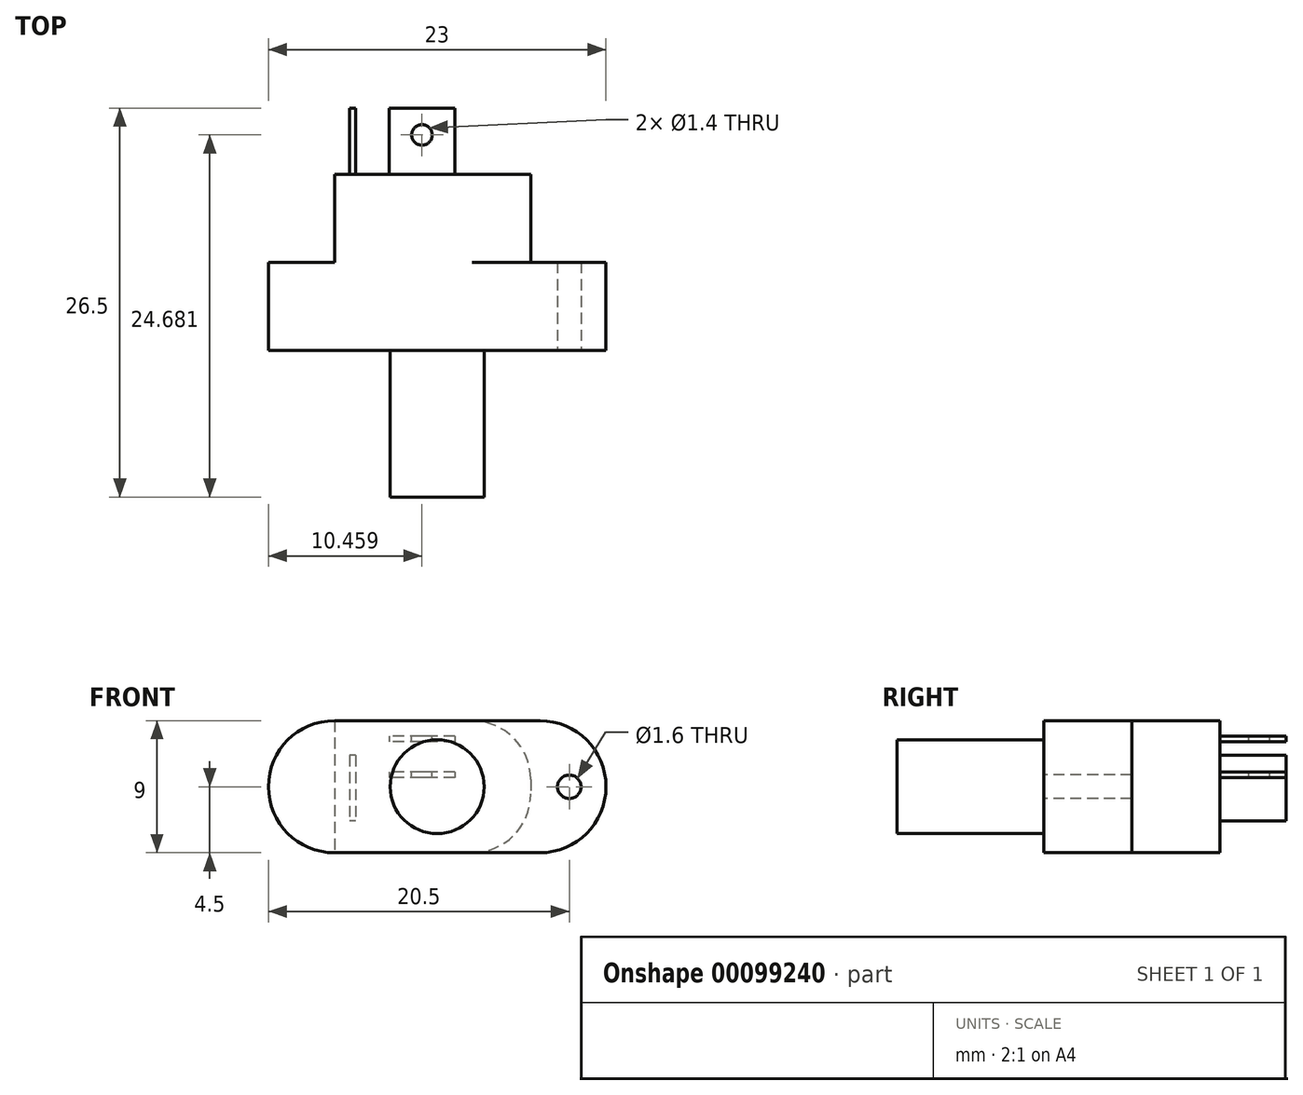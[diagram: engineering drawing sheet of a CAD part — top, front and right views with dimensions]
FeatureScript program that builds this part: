
annotation { "Feature Type Name" : "Feature", "Feature Type Description" : "" }
export const myFeature = defineFeature(function(context is Context, id is Id, definition is map)
    precondition{}
    {
        {
            var Q0;
            Q0=qCreatedBy(makeId("Front.planeOp"),FACE);
            var sketch = newSketch(context, id + "F0", { "sketchPlane" : qUnion([Q0])});
            skLineSegment(sketch, "E0.bottom", {"start": v(7, -4.5) * mm, "end": v(-7, -4.5) * mm});
            skLineSegment(sketch, "E0.top", {"start": v(7, 4.5) * mm, "end": v(-7, 4.5) * mm});
            skLineSegment(sketch, "E0.left", {"start": v(11.5, 0) * mm, "end": v(11.5, 0) * mm});
            skLineSegment(sketch, "E0.right", {"start": v(-11.5, 0) * mm, "end": v(-11.5, 0) * mm});
            skPoint(sketch, "E0.middle", {"position": v(0, 0) * mm});
            skCircle(sketch, "E1", {"center": v(-9, 0) * mm, "radius": 0.8 * mm});
            skCircle(sketch, "E2.MirrorC", {"center": v(9, 0) * mm, "radius": 0.8 * mm});
            skCircle(sketch, "E3", {"center": v(0, 0) * mm, "radius": 3.2 * mm});
            skPoint(sketch, "E4.visualSharp", {"position": v(-11.5, 4.5) * mm});
            skArc(sketch, "E4.filletArc", {"start": v(-7, 4.5) * mm, "mid": v(-10.18, 3.18) * mm, "end": v(-11.5, 0) * mm});
            skPoint(sketch, "E5.visualSharp", {"position": v(-11.5, -4.5) * mm});
            skArc(sketch, "E5.filletArc", {"start": v(-11.5, 0) * mm, "mid": v(-10.18, -3.18) * mm, "end": v(-7, -4.5) * mm});
            skPoint(sketch, "E6.visualSharp", {"position": v(11.5, 4.5) * mm});
            skArc(sketch, "E6.filletArc", {"start": v(11.5, 0) * mm, "mid": v(10.18, 3.18) * mm, "end": v(7, 4.5) * mm});
            skPoint(sketch, "E7.visualSharp", {"position": v(11.5, -4.5) * mm});
            skArc(sketch, "E7.filletArc", {"start": v(7, -4.5) * mm, "mid": v(10.18, -3.18) * mm, "end": v(11.5, 0) * mm});
            skCircle(sketch, "E8", {"center": v(0, 0) * mm, "radius": 1 * mm});
            skSolve(sketch);
        }
        {
            var Q0;
            Q0=makeQuery(id+"F0.imprint","IMPRINT",FACE,{"disambiguationData":[TD([[makeQuery(id+"F0.imprint","IMPRINT",EDGE,{"derivedFrom":sQuery(id+"F0.wireOp",EDGE,"E0.bottom")}),-1.0]])]});
            var Q1;
            Q1=makeQuery(id+"F0.imprint","IMPRINT",FACE,{"disambiguationData":[TD([[makeQuery(id+"F0.imprint","IMPRINT",EDGE,{"derivedFrom":sQuery(id+"F0.wireOp",EDGE,"E3")}),1.0]])]});
            var Q2;
            Q2=makeQuery(id+"F0.imprint","IMPRINT",FACE,{"disambiguationData":[TD([[makeQuery(id+"F0.imprint","IMPRINT",EDGE,{"derivedFrom":sQuery(id+"F0.wireOp",EDGE,"E8")}),1.0]])]});
            var Q3;
            Q3=makeQuery(id+"F0.imprint","IMPRINT",FACE,{"disambiguationData":[TD([[makeQuery(id+"F0.imprint","IMPRINT",EDGE,{"derivedFrom":sQuery(id+"F0.wireOp",EDGE,"E2.MirrorC")}),-1.0]])]});
            var Q4;
            Q4=makeQuery(id+"F0.imprint","IMPRINT",FACE,{"disambiguationData":[TD([[makeQuery(id+"F0.imprint","IMPRINT",EDGE,{"derivedFrom":sQuery(id+"F0.wireOp",EDGE,"E1")}),1.0]])]});
            extrude(context, id + "F1", {"entities" : qUnion([Q0, Q1, Q2, Q3, Q4]), "oppositeDirection" : true, "depth" : 6 * mm});
        }
        {
            var Q0;
            Q0=makeQuery(id+"F1.opExtrude","CAP_FACE",FACE,{"disambiguationData":[OSD([sQuery(id+"F0.wireOp",EDGE,"E0.bottom"),sQuery(id+"F0.wireOp",EDGE,"E0.top"),sQuery(id+"F0.wireOp",EDGE,"E1"),sQuery(id+"F0.wireOp",EDGE,"E2.MirrorC"),sQuery(id+"F0.wireOp",EDGE,"E3"),sQuery(id+"F0.wireOp",EDGE,"E4.filletArc"),sQuery(id+"F0.wireOp",EDGE,"E5.filletArc"),sQuery(id+"F0.wireOp",EDGE,"E6.filletArc"),sQuery(id+"F0.wireOp",EDGE,"E7.filletArc")])],"isStart":false});
            var sketch = newSketch(context, id + "F2", { "sketchPlane" : qUnion([Q0])});
            skLineSegment(sketch, "E9.bottom", {"start": v(-2.37, 4.5) * mm, "end": v(7, 4.5) * mm});
            skLineSegment(sketch, "E9.top", {"start": v(-2.37, -4.5) * mm, "end": v(7, -4.5) * mm});
            skLineSegment(sketch, "E9.left", {"start": v(-6.37, 0.5) * mm, "end": v(-6.37, -0.5) * mm});
            skLineSegment(sketch, "E9.right", {"start": v(7, 4.5) * mm, "end": v(7, -4.5) * mm});
            skPoint(sketch, "E10.visualSharp", {"position": v(-6.37, 4.5) * mm});
            skArc(sketch, "E10.filletArc", {"start": v(-2.37, 4.5) * mm, "mid": v(-5.2, 3.33) * mm, "end": v(-6.37, 0.5) * mm});
            skPoint(sketch, "E11.visualSharp", {"position": v(-6.37, -4.5) * mm});
            skArc(sketch, "E11.filletArc", {"start": v(-6.37, -0.5) * mm, "mid": v(-5.2, -3.33) * mm, "end": v(-2.37, -4.5) * mm});
            skSolve(sketch);
        }
        {
            var Q0;
            Q0=qSketchRegion(id+"F2",true);
            extrude(context, id + "F3", {"entities" : qUnion([Q0]), "operationType" : NewBodyOperationType.ADD, "depth" : 6 * mm});
        }
        {
            var Q0;
            Q0=makeQuery(id+"F3.opExtrude","CAP_FACE",FACE,{"disambiguationData":[OSD([sQuery(id+"F2.wireOp",EDGE,"E9.bottom"),sQuery(id+"F2.wireOp",EDGE,"E9.top"),sQuery(id+"F2.wireOp",EDGE,"E9.left"),sQuery(id+"F2.wireOp",EDGE,"E9.right"),sQuery(id+"F2.wireOp",EDGE,"E10.filletArc"),sQuery(id+"F2.wireOp",EDGE,"E11.filletArc")])],"isStart":false});
            var sketch = newSketch(context, id + "F4", { "sketchPlane" : qUnion([Q0])});
            skLineSegment(sketch, "E12.bottom", {"start": v(-1.2, 3.46) * mm, "end": v(3.27, 3.46) * mm});
            skLineSegment(sketch, "E12.top", {"start": v(-1.2, 3.06) * mm, "end": v(3.27, 3.06) * mm});
            skLineSegment(sketch, "E12.left", {"start": v(-1.2, 3.46) * mm, "end": v(-1.2, 3.06) * mm});
            skLineSegment(sketch, "E12.right", {"start": v(3.27, 3.46) * mm, "end": v(3.27, 3.06) * mm});
            skLineSegment(sketch, "E13.bottom", {"start": v(-1.2, 1) * mm, "end": v(3.27, 1) * mm});
            skLineSegment(sketch, "E13.top", {"start": v(-1.2, 0.6) * mm, "end": v(3.27, 0.6) * mm});
            skLineSegment(sketch, "E13.left", {"start": v(-1.2, 1) * mm, "end": v(-1.2, 0.6) * mm});
            skLineSegment(sketch, "E13.right", {"start": v(3.27, 1) * mm, "end": v(3.27, 0.6) * mm});
            skLineSegment(sketch, "E14.bottom", {"start": v(5.56, 2.14) * mm, "end": v(5.96, 2.14) * mm});
            skLineSegment(sketch, "E14.top", {"start": v(5.56, -2.32) * mm, "end": v(5.96, -2.32) * mm});
            skLineSegment(sketch, "E14.left", {"start": v(5.56, 2.14) * mm, "end": v(5.56, -2.32) * mm});
            skLineSegment(sketch, "E14.right", {"start": v(5.96, 2.14) * mm, "end": v(5.96, -2.32) * mm});
            skSolve(sketch);
        }
        {
            var Q0;
            Q0=qSketchRegion(id+"F4",true);
            var Q1;
            Q1=qConstructionFilter(qBodyType(qCreatedBy(id+"F4",EDGE),BodyType.WIRE),ConstructionObject.NO);
            extrude(context, id + "F5", {"entities" : qUnion([Q0]), "operationType" : NewBodyOperationType.ADD, "surfaceEntities" : qUnion([Q1]), "depth" : 4.5 * mm});
        }
        {
            var Q0;
            Q0=makeQuery(id+"F5.opExtrude","SWEPT_FACE",FACE,{"disambiguationData":[OSD([sQuery(id+"F4.wireOp",EDGE,"E12.bottom")])]});
            var sketch = newSketch(context, id + "F6", { "sketchPlane" : qUnion([Q0])});
            skCircle(sketch, "E15", {"center": v(-1.04, 14.68) * mm, "radius": 0.7 * mm});
            skLineSegment(sketch, "E16", {"start": v(-3.27, 14.68) * mm, "end": v(-1.04, 14.68) * mm, "construction": true});
            skLineSegment(sketch, "E17", {"start": v(-1.04, 14.68) * mm, "end": v(1.2, 14.68) * mm, "construction": true});
            skLineSegment(sketch, "E18", {"start": v(-1.04, 14.68) * mm, "end": v(-1.04, 16.5) * mm, "construction": true});
            skSolve(sketch);
        }
        {
            var Q0;
            Q0=qSketchRegion(id+"F6",true);
            extrude(context, id + "F7", {"entities" : qUnion([Q0]), "operationType" : NewBodyOperationType.REMOVE, "oppositeDirection" : true, "depth" : 5 * mm});
        }
        {
            var Q0;
            Q0=makeQuery(id+"F0.imprint","IMPRINT",FACE,{"disambiguationData":[TD([[makeQuery(id+"F0.imprint","IMPRINT",EDGE,{"derivedFrom":sQuery(id+"F0.wireOp",EDGE,"E8")}),1.0]])]});
            var Q1;
            Q1=makeQuery(id+"F0.imprint","IMPRINT",FACE,{"disambiguationData":[TD([[makeQuery(id+"F0.imprint","IMPRINT",EDGE,{"derivedFrom":sQuery(id+"F0.wireOp",EDGE,"E3")}),1.0]])]});
            var Q2;
            Q2=sQuery(id+"F0.wireOp",EDGE,"E3");
            extrude(context, id + "F8", {"entities" : qUnion([Q0, Q1]), "operationType" : NewBodyOperationType.ADD, "surfaceEntities" : qUnion([Q2]), "depth" : 10 * mm});
        }
    });
